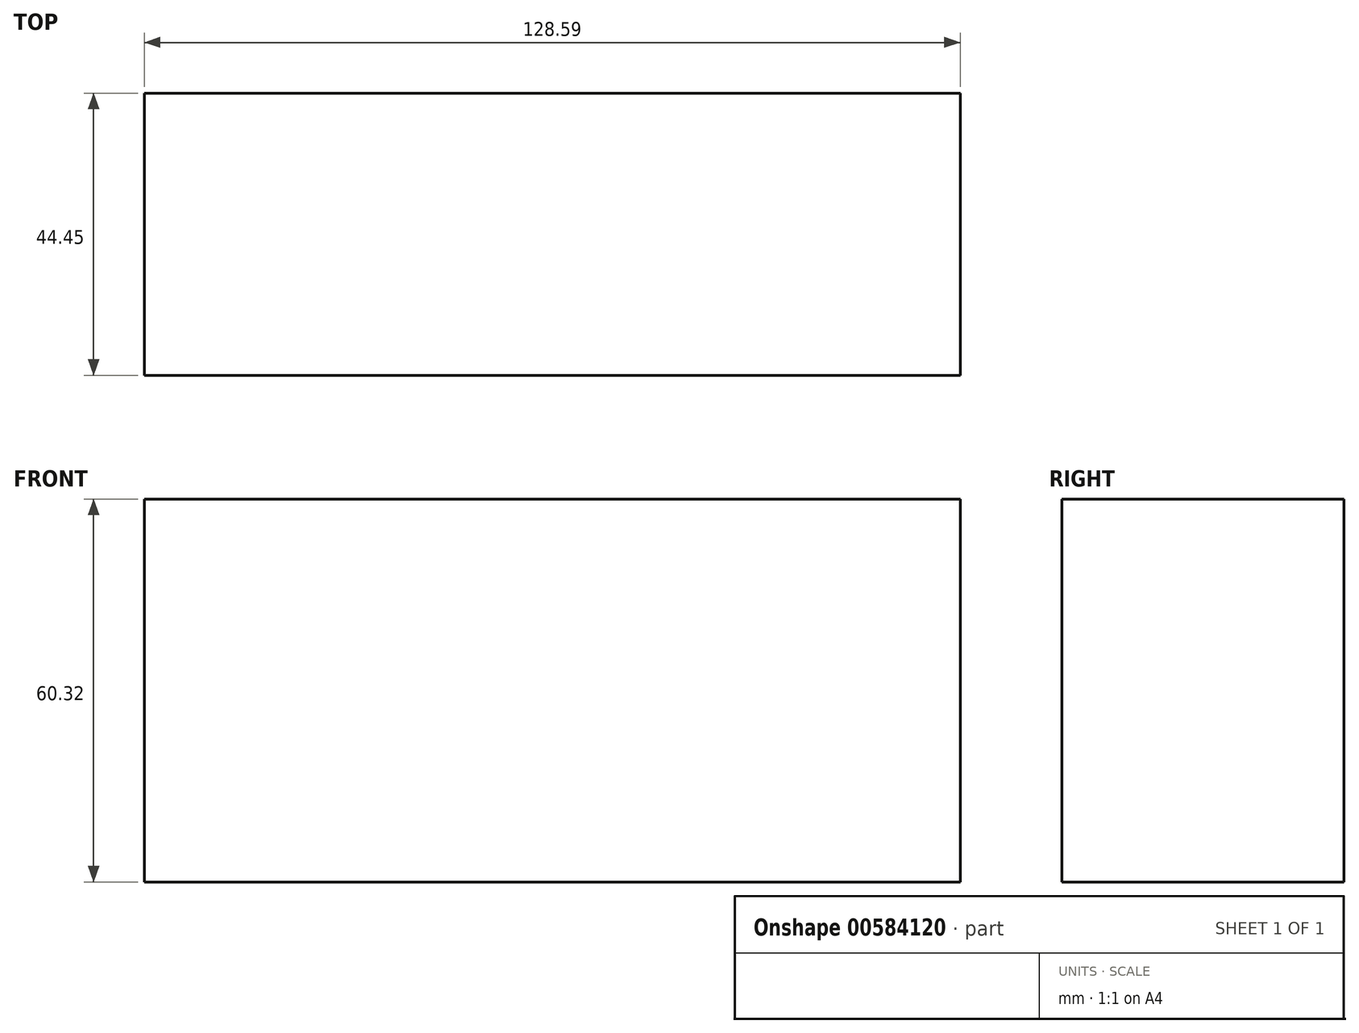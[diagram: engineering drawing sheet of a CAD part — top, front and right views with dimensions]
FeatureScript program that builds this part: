
annotation { "Feature Type Name" : "Feature", "Feature Type Description" : "" }
export const myFeature = defineFeature(function(context is Context, id is Id, definition is map)
    precondition{}
    {
        {
            var Q0;
            Q0=qCreatedBy(makeId("Front.planeOp"),FACE);
            var sketch = newSketch(context, id + "F0", { "sketchPlane" : qUnion([Q0])});
            skLineSegment(sketch, "E0", {"start": v(-54.45, 0) * mm, "end": v(74.14, 0) * mm});
            skLineSegment(sketch, "E1", {"start": v(-54.45, 0) * mm, "end": v(-54.45, 60.33) * mm});
            skLineSegment(sketch, "E2", {"start": v(-54.45, 60.33) * mm, "end": v(74.14, 60.33) * mm});
            skLineSegment(sketch, "E3", {"start": v(74.14, 60.33) * mm, "end": v(74.14, 0) * mm});
            skSolve(sketch);
        }
        {
            var Q0;
            Q0=makeQuery(id+"F0.imprint","IMPRINT",FACE,{"disambiguationData":[TD([[makeQuery(id+"F0.imprint","IMPRINT",EDGE,{"derivedFrom":sQuery(id+"F0.wireOp",EDGE,"E0")}),1.0]])]});
            extrude(context, id + "F1", {"entities" : qUnion([Q0]), "depth" : 44.45 * mm, "offsetDistance" : 25.4 * mm});
        }
    });
